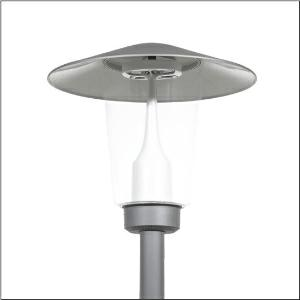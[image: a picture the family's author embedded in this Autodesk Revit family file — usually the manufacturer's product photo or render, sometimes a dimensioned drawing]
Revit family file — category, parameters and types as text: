
# Revit family: pilzleuchte_iq___st1_2a_5xa5235mf14h_7035
name_source: partatom
category: Lighting Fixtures
units: mm (PartAtom-declared; Revit-internal decimal feet)

## family parameters
Cut with Voids When Loaded = No
Host = Face
Light Source = No
Part Type = Normal
Room Calculation Point = No
Round Connector Dimension = Use Diameter
Shared = No

## types (1)
- --- (1 x LED, 1550 lm, 11.8 W, 2700K)
    Apparent Load = 12 VA
    CIE Flux Codes = 24 61 93 98 100
    Color Rendering = 70
    Color Temperature = 2700K
    Default Elevation = 1800 mm
    Description = Mushroom Luminaire iQ, mast luminaire, Module 540 iQ-SR, primary light control with 3 zone facetted reflector, of plastic, silver coated, highly specular, structured, primary optical cover: cover, of PMMA, transparent, light distribution: ST1.2a, light emission: direct distribution, primary light characteristic: asymmetric, installation type: post-top, LED, High Power LED, rated luminous flux: 1.550lm, luminous efficacy: 131lm/W, light colour: 727, colour temperature: 2700K, control gear: ECG iQ, control: presetting dimming logarithmic, Street-Remote, Auto-Match, Temp-Guard, Lumen-Switch, Night-Set, Smart-Wire, Light-Fading, Desk-Remote (wireless, voltage-free reading and setting of iQ features in the workshop via application-optimized NFC function/RFID function), optimised constant luminous flux control (CLO 2.0), with terminal, 6-pole, max. 2.5mm², mains connection: 230..240V, AC, 50/60Hz, start of lifetime: 12W, end of service life: 12W, reduction: 6W, luminaire housing, upper part, of glass-fibre reinforced polyester, coated, Siteco® metallic grey (DB 702S), diameter: 650mm, height: 586mm, spigot size: d x l = 76 x 70mm (post-top) | with reducer (optional accessory) 60 x 70mm, post-top mast mounting element, of diecast aluminium, coated, Siteco® metallic grey (DB 702S), Module 540 iQ-SR, traffic white (RAL 9016), equipment: standard, protection rating (complete): IP65, insulation class (complete): insulation class II (safety insulation), certification: CE, ENEC, VDE, packaging unit: 1 piece

Light Distribution: ST1.2a
    Height = 586 mm
    Lamp = 1 x LED
    Lamp Light Flux = 1550 lm
    Lamp Power = 11.8 W
    Lamp count = 1
    Length = 650 mm
    Luminous efficacy = 131 lm/W
    Manufacturer = Siteco
    ModVariant = No
    Model = 5XA5235MF14H
    Number of Poles = 1
    OnlyDefault = Yes
    Power Factor = 1
    Product Name = Pilzleuchte iQ | ST1.2a
    Product group = mast luminaire | pylon top
    ProductGroupID = 6100
    Protection Class = Protection class II
    Protection Degree = IP 65
    RLX_Detail_Level = 1
    RLX_Emergency_Light_Flux = 0 lm
    RLX_Emergency_Type = 0
    RLX_Emergency_Type_DB = No
    RlxData = <blob elided: 123117 chars, md5=e598f011>
    Socket = socket
    Standby Power = 0 W
    System Light Flux = 1550 lm
    System Power = 12 W
    Type Comments = factory setting: luminous flux: 100 % | dim-lin: 254 | 472 mA
    Type Image = l_1006077.jpg
    URL = http://relux.com
    VarID = @adj_085743
    Voltage = 0 V
    Weight = 0.00 kg
    Width = 0 mm  [stored 0 ft]

note: [stored X ft] marks values corroborated as IEEE doubles in the binary element streams (Revit-internal decimal feet)

## geometry (parser evidence)
native form markers: Blend x4, Sweep x12
no freeform markers — native parametric forms only
